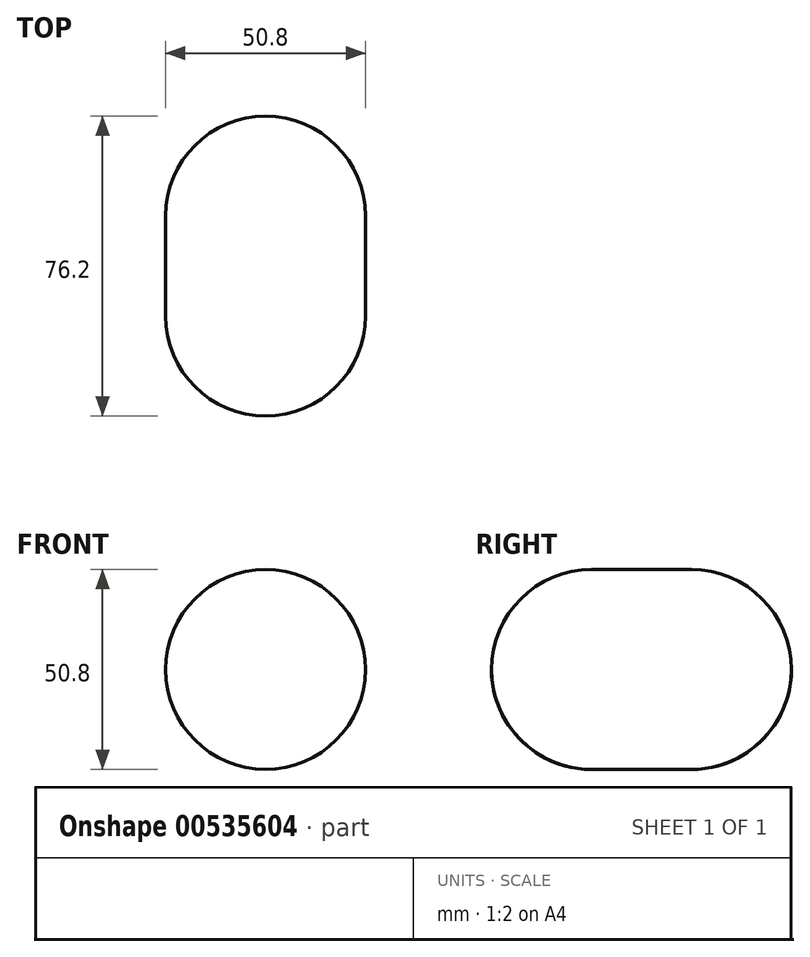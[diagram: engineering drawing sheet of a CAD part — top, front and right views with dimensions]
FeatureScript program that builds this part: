
annotation { "Feature Type Name" : "Feature", "Feature Type Description" : "" }
export const myFeature = defineFeature(function(context is Context, id is Id, definition is map)
    precondition{}
    {
        {
            var Q0;
            Q0=qCreatedBy(makeId("Front.planeOp"),FACE);
            var sketch = newSketch(context, id + "F0", { "sketchPlane" : qUnion([Q0])});
            skCircle(sketch, "E0", {"center": v(0, 0) * mm, "radius": 25.4 * mm});
            skSolve(sketch);
        }
        {
            var Q0;
            Q0 = qSketchRegion(id + "F0", true);
            extrude(context, id + "F1", {"entities" : qUnion([Q0]), "depth" : 50.8 * mm, "offsetDistance" : 25.4 * mm, "hasSecondDirection" : true, "secondDirectionOppositeDirection" : true, "secondDirectionDepth" : 25.4 * mm});
        }
        {
            var Q0;
            Q0=makeQuery(id+"F1.opExtrude","CAP_EDGE",EDGE,{"disambiguationData":[OSD([sQuery(id+"F0.wireOp",EDGE,"E0")])],"isStart":true});
            var Q1;
            Q1=makeQuery(id+"F1.opExtrude","CAP_EDGE",EDGE,{"disambiguationData":[OSD([sQuery(id+"F0.wireOp",EDGE,"E0")])],"isStart":false});
            fillet(context, id + "F2", {"entities" : qUnion([Q0, Q1]), "radius" : 25.4 * mm, "tangentPropagation" : true, "allowEdgeOverflow" : false});
        }
    });
